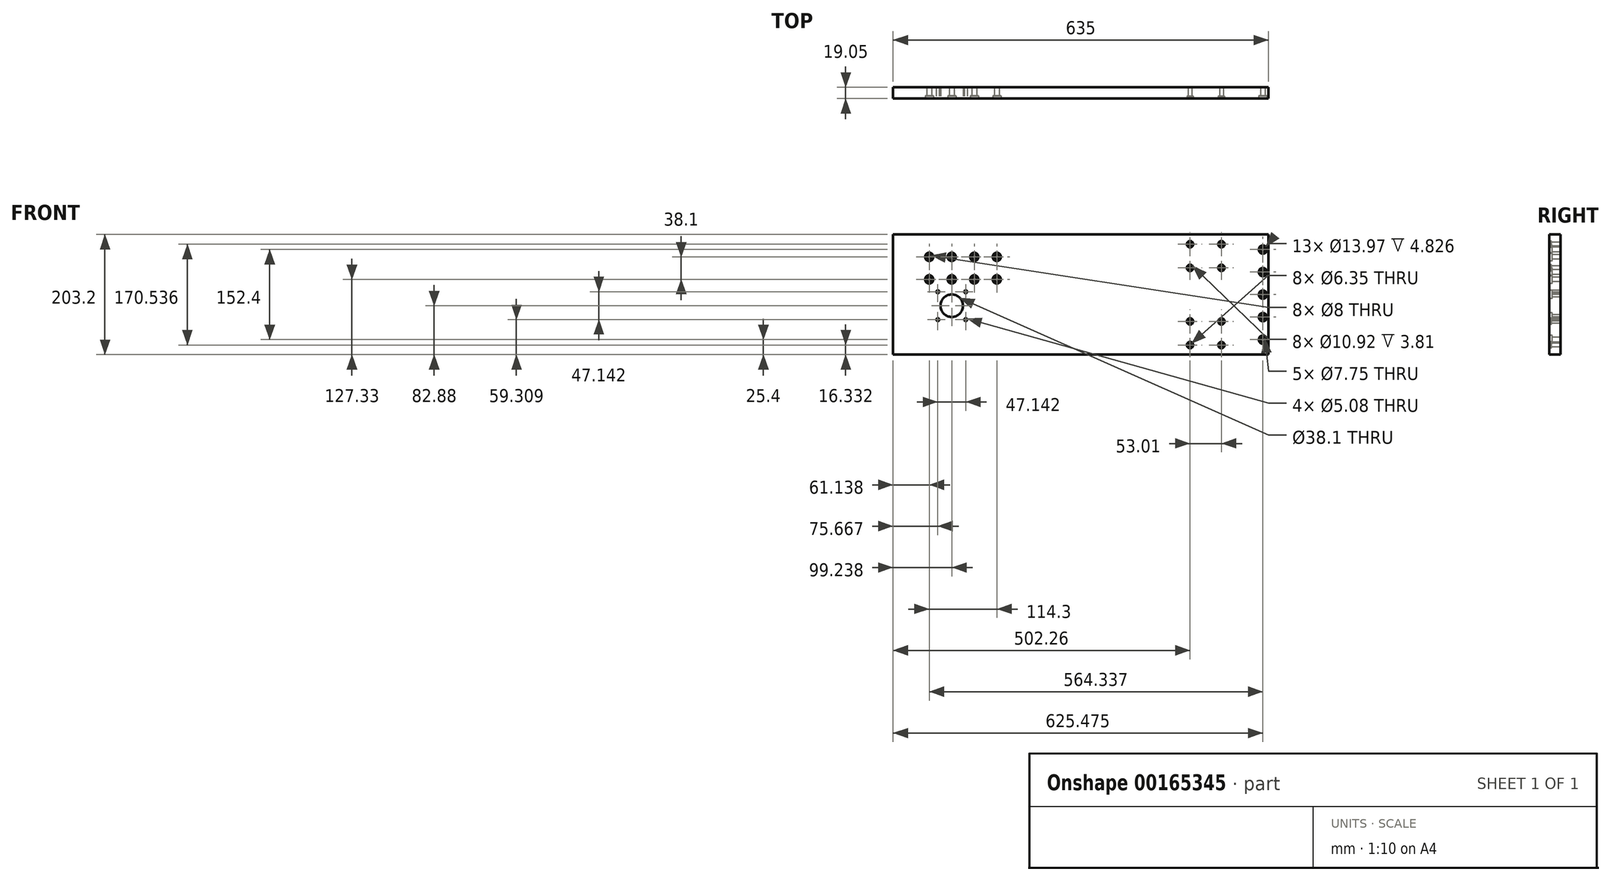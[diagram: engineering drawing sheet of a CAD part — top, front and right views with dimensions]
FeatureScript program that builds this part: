
annotation { "Feature Type Name" : "Feature", "Feature Type Description" : "" }
export const myFeature = defineFeature(function(context is Context, id is Id, definition is map)
    precondition{}
    {
        {
            var Q0;
            Q0=qCreatedBy(makeId("Front.planeOp"),FACE);
            var sketch = newSketch(context, id + "F0", { "sketchPlane" : qUnion([Q0])});
            skLineSegment(sketch, "E0.rect.bottom", {"start": v(317.5, 101.6) * mm, "end": v(-317.5, 101.6) * mm});
            skLineSegment(sketch, "E0.rect.top", {"start": v(317.5, -101.6) * mm, "end": v(-317.5, -101.6) * mm});
            skLineSegment(sketch, "E0.rect.left", {"start": v(317.5, 101.6) * mm, "end": v(317.5, -101.6) * mm});
            skLineSegment(sketch, "E0.rect.right", {"start": v(-317.5, 101.6) * mm, "end": v(-317.5, -101.6) * mm});
            skPoint(sketch, "E0.rect.middle", {"position": v(0, 0) * mm});
            skSolve(sketch);
        }
        {
            var Q0;
            Q0=qSketchRegion(id+"F0",true);
            extrude(context, id + "F1", {"entities" : qUnion([Q0]), "depth" : 19.05 * mm});
        }
        {
            var Q0;
            Q0=makeQuery(id+"F1.opExtrude","CAP_FACE",FACE,{"disambiguationData":[OSD([sQuery(id+"F0.wireOp",EDGE,"E0.rect.bottom"),sQuery(id+"F0.wireOp",EDGE,"E0.rect.top"),sQuery(id+"F0.wireOp",EDGE,"E0.rect.left"),sQuery(id+"F0.wireOp",EDGE,"E0.rect.right")])],"isStart":false});
            var sketch = newSketch(context, id + "F2", { "sketchPlane" : qUnion([Q0])});
            skLineSegment(sketch, "E1", {"start": v(-317.5, 25.73) * mm, "end": v(317.5, 25.73) * mm, "construction": true});
            skLineSegment(sketch, "E2", {"start": v(-256.36, 101.6) * mm, "end": v(-256.36, -101.6) * mm, "construction": true});
            skLineSegment(sketch, "E3", {"start": v(-317.5, 63.83) * mm, "end": v(317.5, 63.83) * mm, "construction": true});
            skLineSegment(sketch, "E4", {"start": v(-218.26, 101.6) * mm, "end": v(-218.26, -101.6) * mm, "construction": true});
            skLineSegment(sketch, "E5", {"start": v(-180.16, 101.6) * mm, "end": v(-180.16, -101.6) * mm, "construction": true});
            skLineSegment(sketch, "E6", {"start": v(-142.06, 101.6) * mm, "end": v(-142.06, -101.6) * mm, "construction": true});
            skCircle(sketch, "E7", {"center": v(-256.36, 63.83) * mm, "radius": 4 * mm});
            skCircle(sketch, "E8", {"center": v(-218.26, 63.83) * mm, "radius": 4 * mm});
            skCircle(sketch, "E9", {"center": v(-180.16, 63.83) * mm, "radius": 4 * mm});
            skCircle(sketch, "E10", {"center": v(-142.06, 63.83) * mm, "radius": 4 * mm});
            skCircle(sketch, "E11", {"center": v(-142.06, 25.73) * mm, "radius": 4 * mm});
            skCircle(sketch, "E12", {"center": v(-180.16, 25.73) * mm, "radius": 4 * mm});
            skCircle(sketch, "E13", {"center": v(-218.26, 25.73) * mm, "radius": 4 * mm});
            skCircle(sketch, "E14", {"center": v(-256.36, 25.73) * mm, "radius": 4 * mm});
            skSolve(sketch);
        }
        {
            var Q0;
            Q0=qSketchRegion(id+"F2",true);
            extrude(context, id + "F3", {"entities" : qUnion([Q0]), "operationType" : NewBodyOperationType.REMOVE, "endBound" : BoundingType.THROUGH_ALL, "oppositeDirection" : true, "depth" : 25.4 * mm});
        }
        {
            var Q0;
            Q0=makeQuery(id+"F1.opExtrude","CAP_FACE",FACE,{"disambiguationData":[OSD([sQuery(id+"F0.wireOp",EDGE,"E0.rect.bottom"),sQuery(id+"F0.wireOp",EDGE,"E0.rect.top"),sQuery(id+"F0.wireOp",EDGE,"E0.rect.left"),sQuery(id+"F0.wireOp",EDGE,"E0.rect.right")])],"isStart":false});
            var sketch = newSketch(context, id + "F4", { "sketchPlane" : qUnion([Q0])});
            skLineSegment(sketch, "E15", {"start": v(-317.5, -18.72) * mm, "end": v(-218.26, -18.72) * mm, "construction": true});
            skLineSegment(sketch, "E16", {"start": v(-218.26, 101.6) * mm, "end": v(-218.26, -101.6) * mm, "construction": true});
            skCircle(sketch, "E17", {"center": v(-218.26, -18.72) * mm, "radius": 19.05 * mm});
            skLineSegment(sketch, "E18.rect.bottom", {"start": v(-194.7, -42.3) * mm, "end": v(-241.83, -42.3) * mm, "construction": true});
            skLineSegment(sketch, "E18.rect.top", {"start": v(-194.7, 4.85) * mm, "end": v(-241.83, 4.85) * mm, "construction": true});
            skLineSegment(sketch, "E18.rect.left", {"start": v(-194.7, -42.3) * mm, "end": v(-194.7, 4.85) * mm, "construction": true});
            skLineSegment(sketch, "E18.rect.right", {"start": v(-241.83, -42.3) * mm, "end": v(-241.83, 4.85) * mm, "construction": true});
            skCircle(sketch, "E19", {"center": v(-241.83, 4.85) * mm, "radius": 2.54 * mm});
            skCircle(sketch, "E20", {"center": v(-194.7, 4.85) * mm, "radius": 2.54 * mm});
            skCircle(sketch, "E21", {"center": v(-194.7, -42.3) * mm, "radius": 2.54 * mm});
            skCircle(sketch, "E22", {"center": v(-241.83, -42.3) * mm, "radius": 2.54 * mm});
            skSolve(sketch);
        }
        {
            var Q0;
            Q0=qSketchRegion(id+"F4",true);
            extrude(context, id + "F5", {"entities" : qUnion([Q0]), "operationType" : NewBodyOperationType.REMOVE, "endBound" : BoundingType.THROUGH_ALL, "oppositeDirection" : true, "depth" : 25.4 * mm});
        }
        {
            var Q0;
            Q0=makeQuery(id+"F1.opExtrude","CAP_FACE",FACE,{"disambiguationData":[OSD([sQuery(id+"F0.wireOp",EDGE,"E0.rect.bottom"),sQuery(id+"F0.wireOp",EDGE,"E0.rect.top"),sQuery(id+"F0.wireOp",EDGE,"E0.rect.left"),sQuery(id+"F0.wireOp",EDGE,"E0.rect.right")])],"isStart":false});
            var sketch = newSketch(context, id + "F6", { "sketchPlane" : qUnion([Q0])});
            skLineSegment(sketch, "E23", {"start": v(-317.5, 85.27) * mm, "end": v(317.5, 85.27) * mm, "construction": true});
            skLineSegment(sketch, "E24", {"start": v(-317.5, -85.27) * mm, "end": v(317.5, -85.27) * mm, "construction": true});
            skLineSegment(sketch, "E25", {"start": v(-317.5, 45.26) * mm, "end": v(317.5, 45.26) * mm, "construction": true});
            skLineSegment(sketch, "E26", {"start": v(-317.5, -45.26) * mm, "end": v(317.5, -45.26) * mm, "construction": true});
            skLineSegment(sketch, "E27", {"start": v(184.76, 101.6) * mm, "end": v(184.76, -101.6) * mm, "construction": true});
            skLineSegment(sketch, "E28", {"start": v(237.77, 101.6) * mm, "end": v(237.77, -101.6) * mm, "construction": true});
            skCircle(sketch, "E29", {"center": v(184.76, 85.27) * mm, "radius": 3.18 * mm});
            skCircle(sketch, "E30", {"center": v(237.77, 85.27) * mm, "radius": 3.18 * mm});
            skCircle(sketch, "E31", {"center": v(184.76, 45.26) * mm, "radius": 3.18 * mm});
            skCircle(sketch, "E32", {"center": v(237.77, 45.26) * mm, "radius": 3.18 * mm});
            skCircle(sketch, "E33", {"center": v(184.76, -45.26) * mm, "radius": 3.18 * mm});
            skCircle(sketch, "E34", {"center": v(237.77, -45.26) * mm, "radius": 3.18 * mm});
            skCircle(sketch, "E35", {"center": v(184.76, -85.27) * mm, "radius": 3.18 * mm});
            skCircle(sketch, "E36", {"center": v(237.77, -85.27) * mm, "radius": 3.18 * mm});
            skSolve(sketch);
        }
        {
            var Q0;
            Q0=qSketchRegion(id+"F6",true);
            extrude(context, id + "F7", {"entities" : qUnion([Q0]), "operationType" : NewBodyOperationType.REMOVE, "endBound" : BoundingType.THROUGH_ALL, "oppositeDirection" : true, "depth" : 25.4 * mm});
        }
        {
            var Q0;
            Q0=makeQuery(id+"F1.opExtrude","CAP_FACE",FACE,{"disambiguationData":[OSD([sQuery(id+"F0.wireOp",EDGE,"E0.rect.bottom"),sQuery(id+"F0.wireOp",EDGE,"E0.rect.top"),sQuery(id+"F0.wireOp",EDGE,"E0.rect.left"),sQuery(id+"F0.wireOp",EDGE,"E0.rect.right")])],"isStart":false});
            var sketch = newSketch(context, id + "F8", { "sketchPlane" : qUnion([Q0])});
            skLineSegment(sketch, "E37", {"start": v(307.98, 101.6) * mm, "end": v(307.98, -101.6) * mm, "construction": true});
            skLineSegment(sketch, "E38", {"start": v(-317.5, 76.2) * mm, "end": v(317.5, 76.2) * mm, "construction": true});
            skLineSegment(sketch, "E39", {"start": v(-317.5, 38.1) * mm, "end": v(317.5, 38.1) * mm, "construction": true});
            skLineSegment(sketch, "E40", {"start": v(-317.5, 0) * mm, "end": v(317.5, 0) * mm, "construction": true});
            skLineSegment(sketch, "E41", {"start": v(-317.5, -38.1) * mm, "end": v(317.5, -38.1) * mm, "construction": true});
            skLineSegment(sketch, "E42", {"start": v(-317.5, -76.2) * mm, "end": v(317.5, -76.2) * mm, "construction": true});
            skLineSegment(sketch, "E43", {"start": v(317.5, 101.6) * mm, "end": v(317.5, -101.6) * mm, "construction": true});
            skCircle(sketch, "E44", {"center": v(307.98, 76.2) * mm, "radius": 3.87 * mm});
            skCircle(sketch, "E45", {"center": v(307.98, 38.1) * mm, "radius": 3.87 * mm});
            skCircle(sketch, "E46", {"center": v(307.98, 0) * mm, "radius": 3.87 * mm});
            skCircle(sketch, "E47", {"center": v(307.98, -38.1) * mm, "radius": 3.87 * mm});
            skCircle(sketch, "E48", {"center": v(307.98, -76.2) * mm, "radius": 3.87 * mm});
            skSolve(sketch);
        }
        {
            var Q0;
            Q0=qSketchRegion(id+"F8",true);
            extrude(context, id + "F9", {"entities" : qUnion([Q0]), "operationType" : NewBodyOperationType.REMOVE, "endBound" : BoundingType.THROUGH_ALL, "oppositeDirection" : true, "depth" : 25.4 * mm});
        }
        {
            var Q0;
            Q0=makeQuery(id+"F1.opExtrude","CAP_FACE",FACE,{"disambiguationData":[OSD([sQuery(id+"F0.wireOp",EDGE,"E0.rect.bottom"),sQuery(id+"F0.wireOp",EDGE,"E0.rect.top"),sQuery(id+"F0.wireOp",EDGE,"E0.rect.left"),sQuery(id+"F0.wireOp",EDGE,"E0.rect.right")])],"isStart":false});
            var sketch = newSketch(context, id + "F10", { "sketchPlane" : qUnion([Q0])});
            skCircle(sketch, "E49", {"center": v(-256.36, 63.83) * mm, "radius": 6.99 * mm});
            skCircle(sketch, "E50", {"center": v(-256.36, 25.73) * mm, "radius": 6.99 * mm});
            skCircle(sketch, "E51", {"center": v(-218.26, 25.73) * mm, "radius": 6.99 * mm});
            skCircle(sketch, "E52", {"center": v(-218.26, 63.83) * mm, "radius": 6.99 * mm});
            skCircle(sketch, "E53", {"center": v(-180.16, 63.83) * mm, "radius": 6.99 * mm});
            skCircle(sketch, "E54", {"center": v(-142.06, 63.83) * mm, "radius": 6.99 * mm});
            skCircle(sketch, "E55", {"center": v(-180.16, 25.73) * mm, "radius": 6.99 * mm});
            skCircle(sketch, "E56", {"center": v(-142.06, 25.73) * mm, "radius": 6.99 * mm});
            skCircle(sketch, "E57", {"center": v(307.98, -76.2) * mm, "radius": 6.99 * mm});
            skCircle(sketch, "E58", {"center": v(307.98, -38.1) * mm, "radius": 6.99 * mm});
            skCircle(sketch, "E59", {"center": v(307.98, 0) * mm, "radius": 6.99 * mm});
            skCircle(sketch, "E60", {"center": v(307.98, 38.1) * mm, "radius": 6.99 * mm});
            skCircle(sketch, "E61", {"center": v(307.98, 76.2) * mm, "radius": 6.99 * mm});
            skSolve(sketch);
        }
        {
            var Q0;
            Q0 = qSketchRegion(id + "F10", true);
            extrude(context, id + "F11", {"entities" : qUnion([Q0]), "operationType" : NewBodyOperationType.REMOVE, "oppositeDirection" : true, "depth" : 4.83 * mm});
        }
        {
            var Q0;
            Q0=makeQuery(id+"F1.opExtrude","CAP_FACE",FACE,{"disambiguationData":[OSD([sQuery(id+"F0.wireOp",EDGE,"E0.rect.bottom"),sQuery(id+"F0.wireOp",EDGE,"E0.rect.top"),sQuery(id+"F0.wireOp",EDGE,"E0.rect.left"),sQuery(id+"F0.wireOp",EDGE,"E0.rect.right")])],"isStart":false});
            var sketch = newSketch(context, id + "F12", { "sketchPlane" : qUnion([Q0])});
            skCircle(sketch, "E62", {"center": v(184.76, 85.27) * mm, "radius": 5.46 * mm});
            skCircle(sketch, "E63", {"center": v(184.76, 45.26) * mm, "radius": 5.46 * mm});
            skCircle(sketch, "E64", {"center": v(184.76, -45.26) * mm, "radius": 5.46 * mm});
            skCircle(sketch, "E65", {"center": v(184.76, -85.27) * mm, "radius": 5.46 * mm});
            skCircle(sketch, "E66", {"center": v(237.77, -85.27) * mm, "radius": 5.46 * mm});
            skCircle(sketch, "E67", {"center": v(237.77, -45.26) * mm, "radius": 5.46 * mm});
            skCircle(sketch, "E68", {"center": v(237.77, 45.26) * mm, "radius": 5.46 * mm});
            skCircle(sketch, "E69", {"center": v(237.77, 85.27) * mm, "radius": 5.46 * mm});
            skSolve(sketch);
        }
        {
            var Q0;
            Q0 = qSketchRegion(id + "F12", true);
            extrude(context, id + "F13", {"entities" : qUnion([Q0]), "operationType" : NewBodyOperationType.REMOVE, "oppositeDirection" : true, "depth" : 3.8 * mm});
        }
    });
